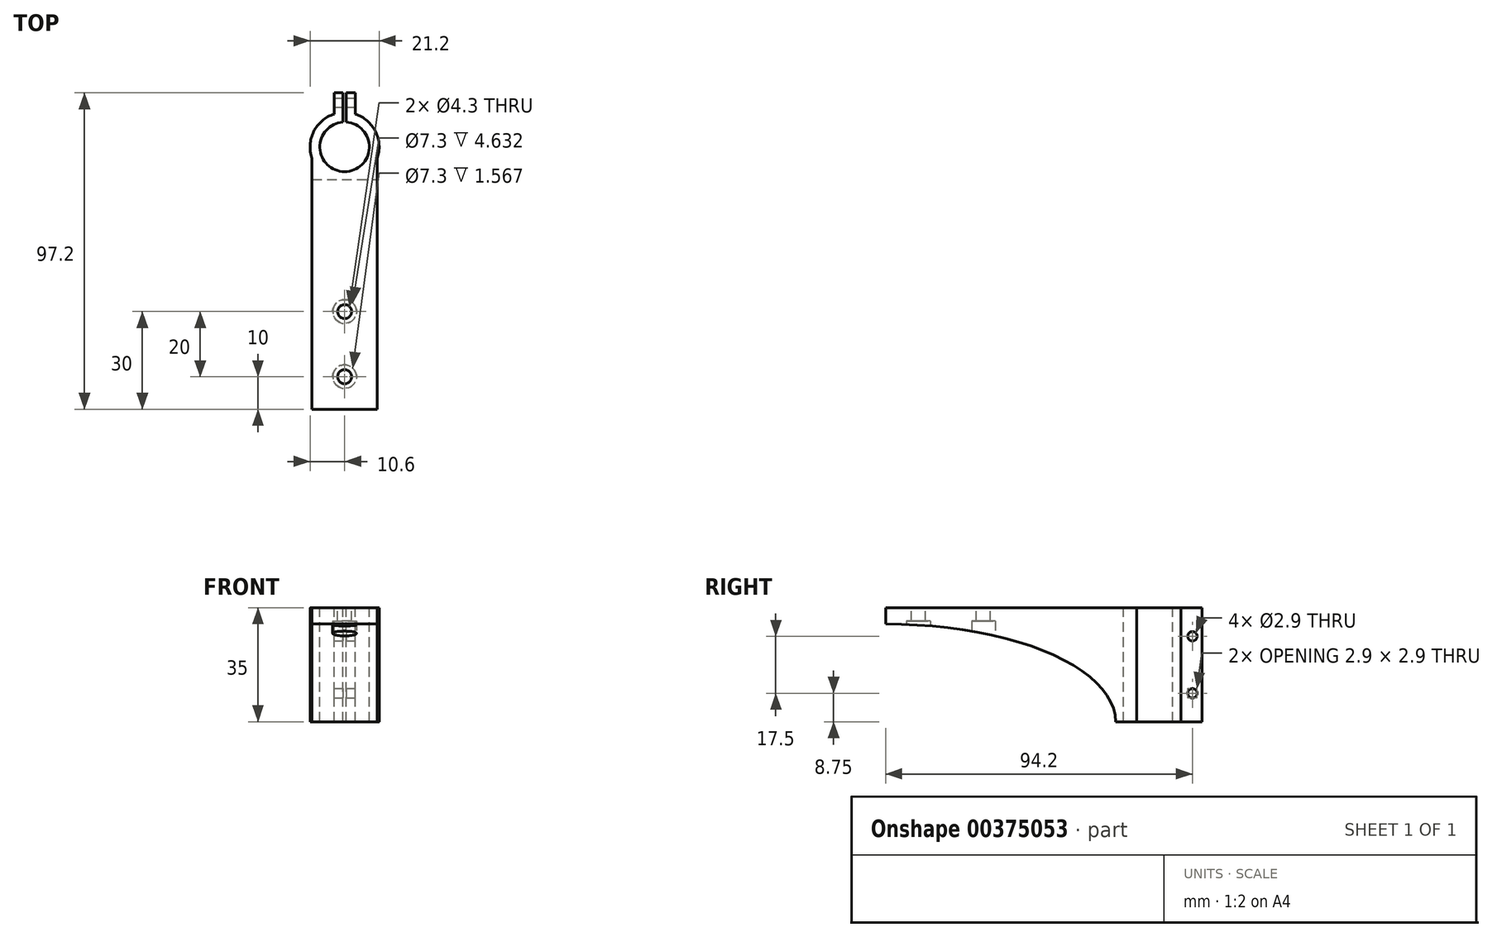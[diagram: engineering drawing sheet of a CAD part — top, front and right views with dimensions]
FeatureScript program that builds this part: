
annotation { "Feature Type Name" : "Feature", "Feature Type Description" : "" }
export const myFeature = defineFeature(function(context is Context, id is Id, definition is map)
    precondition{}
    {
        {
            var Q0;
            Q0=qCreatedBy(makeId("Top.planeOp"),FACE);
            var sketch = newSketch(context, id + "F0", { "sketchPlane" : qUnion([Q0])});
            skCircle(sketch, "E0", {"center": v(0, 0) * mm, "radius": 7.6 * mm});
            skArc(sketch, "E1.0", {"start": v(-3.25, 10.09) * mm, "mid": v(0, -10.6) * mm, "end": v(3.25, 10.09) * mm});
            skLineSegment(sketch, "E2.top", {"start": v(3.25, 16.6) * mm, "end": v(-3.25, 16.6) * mm});
            skLineSegment(sketch, "E2.left", {"start": v(3.25, 10.09) * mm, "end": v(3.25, 16.6) * mm});
            skLineSegment(sketch, "E2.right", {"start": v(-3.25, 10.09) * mm, "end": v(-3.25, 16.6) * mm});
            skPoint(sketch, "E2.middle", {"position": v(0, 10.6) * mm});
            skLineSegment(sketch, "E3.top", {"start": v(-10, -80.6) * mm, "end": v(10, -80.6) * mm});
            skLineSegment(sketch, "E3.left", {"start": v(-10, -3.52) * mm, "end": v(-10, -80.6) * mm});
            skLineSegment(sketch, "E3.right", {"start": v(10, -3.52) * mm, "end": v(10, -80.6) * mm});
            skSolve(sketch);
        }
        {
            var Q0;
            Q0=makeQuery(id+"F0.imprint","IMPRINT",FACE,{"disambiguationData":[TD([[makeQuery(id+"F0.imprint","IMPRINT",EDGE,{"derivedFrom":sQuery(id+"F0.wireOp",EDGE,"E3.top")}),1.0]])]});
            extrude(context, id + "F1", {"entities" : qUnion([Q0]), "oppositeDirection" : true, "depth" : 35 * mm});
        }
        {
            var Q0;
            Q0=makeQuery(id+"F0.imprint","IMPRINT",FACE,{"disambiguationData":[TD([[makeQuery(id+"F0.imprint","IMPRINT",EDGE,{"derivedFrom":sQuery(id+"F0.wireOp",EDGE,"E0")}),-1.0]])]});
            extrude(context, id + "F2", {"entities" : qUnion([Q0]), "operationType" : NewBodyOperationType.ADD, "oppositeDirection" : true, "depth" : 35 * mm});
        }
        {
            var Q0;
            {var subQ0=sQuery(id+"F0.wireOp",EDGE,"E1.0");Q0=makeQuery(id+"F2.boolean.opBoolean","MERGE",FACE,{"derivedFrom":[makeQuery(id+"F1.opExtrude","CAP_FACE",FACE,{"disambiguationData":[OSD([subQ0,sQuery(id+"F0.wireOp",EDGE,"E3.top"),sQuery(id+"F0.wireOp",EDGE,"E3.left"),sQuery(id+"F0.wireOp",EDGE,"E3.right")])],"isStart":true}),makeQuery(id+"F2.opExtrude","CAP_FACE",FACE,{"disambiguationData":[OSD([sQuery(id+"F0.wireOp",EDGE,"E0"),subQ0,sQuery(id+"F0.wireOp",EDGE,"E2.top"),sQuery(id+"F0.wireOp",EDGE,"E2.left"),sQuery(id+"F0.wireOp",EDGE,"E2.right")])],"isStart":true})]});}
            var sketch = newSketch(context, id + "F3", { "sketchPlane" : qUnion([Q0])});
            skCircle(sketch, "E4", {"center": v(0, -50.6) * mm, "radius": 2.15 * mm});
            skCircle(sketch, "E5", {"center": v(0, -70.6) * mm, "radius": 2.15 * mm});
            skSolve(sketch);
        }
        {
            var Q0;
            Q0=qSketchRegion(id+"F3",true);
            extrude(context, id + "F4", {"entities" : qUnion([Q0]), "operationType" : NewBodyOperationType.REMOVE, "endBound" : BoundingType.THROUGH_ALL, "oppositeDirection" : true, "depth" : 25 * mm});
        }
        {
            var Q0;
            Q0=makeQuery(id+"F1.opExtrude","CAP_FACE",FACE,{"disambiguationData":[OSD([sQuery(id+"F0.wireOp",EDGE,"E0"),sQuery(id+"F0.wireOp",EDGE,"E1.0"),sQuery(id+"F0.wireOp",EDGE,"E2.top"),sQuery(id+"F0.wireOp",EDGE,"E2.left"),sQuery(id+"F0.wireOp",EDGE,"E2.right"),sQuery(id+"F0.wireOp",EDGE,"E3.top"),sQuery(id+"F0.wireOp",EDGE,"E3.left"),sQuery(id+"F0.wireOp",EDGE,"E3.right")])],"isStart":false});
            var sketch = newSketch(context, id + "F5", { "sketchPlane" : qUnion([Q0])});
            skCircle(sketch, "E6", {"center": v(0, 70.6) * mm, "radius": 3.65 * mm});
            skCircle(sketch, "E7", {"center": v(0, 50.6) * mm, "radius": 3.65 * mm});
            skSolve(sketch);
        }
        {
            var Q0;
            Q0=makeQuery(id+"F5.imprint","IMPRINT",FACE,{"disambiguationData":[TD([[makeQuery(id+"F5.imprint","IMPRINT",EDGE,{"derivedFrom":sQuery(id+"F5.wireOp",EDGE,"E6")}),1.0]])]});
            var Q1;
            Q1=makeQuery(id+"F5.imprint","IMPRINT",FACE,{"disambiguationData":[TD([[makeQuery(id+"F5.imprint","IMPRINT",EDGE,{"derivedFrom":sQuery(id+"F5.wireOp",EDGE,"E7")}),1.0]])]});
            extrude(context, id + "F6", {"entities" : qUnion([Q0, Q1]), "operationType" : NewBodyOperationType.REMOVE, "oppositeDirection" : true, "depth" : 31 * mm});
        }
        {
            var Q0;
            Q0=makeQuery(id+"F1.opExtrude","SWEPT_FACE",FACE,{"disambiguationData":[OSD([sQuery(id+"F0.wireOp",EDGE,"E3.right")])]});
            var sketch = newSketch(context, id + "F7", { "sketchPlane" : qUnion([Q0])});
            skLineSegment(sketch, "E8", {"start": v(-3.52, -35) * mm, "end": v(-10.02, -35) * mm});
            skLineSegment(sketch, "E9", {"start": v(-80.6, 0) * mm, "end": v(-80.6, -5) * mm});
            skEllipse(sketch, "E10", {"center": v(-80.6, -35) * mm, "majorRadius": 70.58 * mm, "minorRadius": 30 * mm, "majorAxis": v(1, 0)});
            skSolve(sketch);
        }
        {
            var Q0;
            {var subQ1=sQuery(id+"F0.wireOp",EDGE,"E3.right");var subQ2=makeQuery(id+"F1.opExtrude","SWEPT_EDGE",EDGE,{"disambiguationData":[OSD([sQuery(id+"F0.wireOp",EDGE,"E3.top"),subQ1])]});var subQ4=makeQuery(id+"F1.opExtrude","CAP_EDGE",EDGE,{"disambiguationData":[OSD([subQ1])],"isStart":false});var subQ6=makeQuery(id+"F7.imprint","INTERSECT",VERTEX,{"derivedFrom":[subQ2,subQ4]});Q0=makeQuery(id+"F7.imprint","IMPRINT",FACE,{"disambiguationData":[TD([[makeQuery(id+"F7.imprint","IMPRINT",EDGE,{"disambiguationData":[TD([[subQ6,1.0]])],"derivedFrom":subQ4}),-1.0]])]});}
            extrude(context, id + "F8", {"entities" : qUnion([Q0]), "operationType" : NewBodyOperationType.REMOVE, "endBound" : BoundingType.THROUGH_ALL, "oppositeDirection" : true, "depth" : 25 * mm});
        }
        {
            var Q0;
            Q0=makeQuery(id+"F1.opExtrude","CAP_FACE",FACE,{"disambiguationData":[OSD([sQuery(id+"F0.wireOp",EDGE,"E0"),sQuery(id+"F0.wireOp",EDGE,"E1.0"),sQuery(id+"F0.wireOp",EDGE,"E2.top"),sQuery(id+"F0.wireOp",EDGE,"E2.left"),sQuery(id+"F0.wireOp",EDGE,"E2.right"),sQuery(id+"F0.wireOp",EDGE,"E3.top"),sQuery(id+"F0.wireOp",EDGE,"E3.left"),sQuery(id+"F0.wireOp",EDGE,"E3.right")])],"isStart":true});
            var sketch = newSketch(context, id + "F9", { "sketchPlane" : qUnion([Q0])});
            skLineSegment(sketch, "E11.bottom", {"start": v(0, 18.6) * mm, "end": v(-0.5, 18.6) * mm});
            skLineSegment(sketch, "E11.top", {"start": v(0, 0) * mm, "end": v(-0.5, 0) * mm});
            skLineSegment(sketch, "E11.left", {"start": v(0, 18.6) * mm, "end": v(0, 0) * mm});
            skLineSegment(sketch, "E11.right", {"start": v(-0.5, 18.6) * mm, "end": v(-0.5, 0) * mm});
            skLineSegment(sketch, "E12.MirrorCS", {"start": v(0.5, 18.6) * mm, "end": v(0.5, 0) * mm});
            skLineSegment(sketch, "E13.MirrorCS", {"start": v(0, 0) * mm, "end": v(0.5, 0) * mm});
            skLineSegment(sketch, "E14.MirrorCS", {"start": v(0, 18.6) * mm, "end": v(0.5, 18.6) * mm});
            skSolve(sketch);
        }
        {
            var Q0;
            {var subQ0=sQuery(id+"F9.wireOp",EDGE,"E11.left");var subQ1=makeQuery(id+"F2.opExtrude","CAP_EDGE",EDGE,{"disambiguationData":[OSD([sQuery(id+"F0.wireOp",EDGE,"E2.top")])],"isStart":true});var subQ2=makeQuery(id+"F9.imprint","INTERSECT",VERTEX,{"derivedFrom":[subQ1,subQ0]});Q0=makeQuery(id+"F9.imprint","IMPRINT",FACE,{"disambiguationData":[TD([[makeQuery(id+"F9.imprint","IMPRINT",EDGE,{"disambiguationData":[TD([[subQ2,-1.0]])],"derivedFrom":subQ0}),1.0]])]});}
            var Q1;
            {var subQ0=sQuery(id+"F9.wireOp",EDGE,"E11.top");Q1=makeQuery(id+"F9.imprint","IMPRINT",FACE,{"disambiguationData":[TD([[makeQuery(id+"F9.imprint","IMPRINT",EDGE,{"derivedFrom":subQ0}),-1.0]])]});}
            var Q2;
            {var subQ0=sQuery(id+"F9.wireOp",EDGE,"E11.bottom");Q2=makeQuery(id+"F9.imprint","IMPRINT",FACE,{"disambiguationData":[TD([[makeQuery(id+"F9.imprint","IMPRINT",EDGE,{"derivedFrom":subQ0}),1.0]])]});}
            var Q3;
            {var subQ0=sQuery(id+"F9.wireOp",EDGE,"E14.MirrorCS");Q3=makeQuery(id+"F9.imprint","IMPRINT",FACE,{"disambiguationData":[TD([[makeQuery(id+"F9.imprint","IMPRINT",EDGE,{"derivedFrom":subQ0}),-1.0]])]});}
            var Q4;
            {var subQ0=sQuery(id+"F9.wireOp",EDGE,"E13.MirrorCS");Q4=makeQuery(id+"F9.imprint","IMPRINT",FACE,{"disambiguationData":[TD([[makeQuery(id+"F9.imprint","IMPRINT",EDGE,{"derivedFrom":subQ0}),1.0]])]});}
            var Q5;
            {var subQ0=sQuery(id+"F9.wireOp",EDGE,"E11.left");var subQ1=makeQuery(id+"F2.opExtrude","CAP_EDGE",EDGE,{"disambiguationData":[OSD([sQuery(id+"F0.wireOp",EDGE,"E2.top")])],"isStart":true});var subQ2=makeQuery(id+"F9.imprint","INTERSECT",VERTEX,{"derivedFrom":[subQ1,subQ0]});Q5=makeQuery(id+"F9.imprint","IMPRINT",FACE,{"disambiguationData":[TD([[makeQuery(id+"F9.imprint","IMPRINT",EDGE,{"disambiguationData":[TD([[subQ2,-1.0]])],"derivedFrom":subQ0}),-1.0]])]});}
            extrude(context, id + "F10", {"entities" : qUnion([Q0, Q1, Q2, Q3, Q4, Q5]), "operationType" : NewBodyOperationType.REMOVE, "endBound" : BoundingType.THROUGH_ALL, "oppositeDirection" : true, "depth" : 25 * mm});
        }
        {
            var Q0;
            Q0=makeQuery(id+"F2.opExtrude","SWEPT_FACE",FACE,{"disambiguationData":[OSD([sQuery(id+"F0.wireOp",EDGE,"E2.left")])]});
            var sketch = newSketch(context, id + "F11", { "sketchPlane" : qUnion([Q0])});
            skCircle(sketch, "E15", {"center": v(13.6, -8.75) * mm, "radius": 1.45 * mm});
            skCircle(sketch, "E16", {"center": v(13.6, -26.25) * mm, "radius": 1.45 * mm});
            skCircle(sketch, "E17.0", {"center": v(13.6, -8.75) * mm, "radius": 2.45 * mm});
            skCircle(sketch, "E18.0", {"center": v(13.6, -26.25) * mm, "radius": 2.45 * mm});
            skSolve(sketch);
        }
        {
            var Q0;
            Q0=makeQuery(id+"F11.imprint","IMPRINT",FACE,{"disambiguationData":[TD([[makeQuery(id+"F11.imprint","IMPRINT",EDGE,{"derivedFrom":sQuery(id+"F11.wireOp",EDGE,"E15")}),1.0]])]});
            var Q1;
            Q1=makeQuery(id+"F11.imprint","IMPRINT",FACE,{"disambiguationData":[TD([[makeQuery(id+"F11.imprint","IMPRINT",EDGE,{"derivedFrom":sQuery(id+"F11.wireOp",EDGE,"E16")}),1.0]])]});
            extrude(context, id + "F12", {"entities" : qUnion([Q0, Q1]), "operationType" : NewBodyOperationType.REMOVE, "endBound" : BoundingType.THROUGH_ALL, "oppositeDirection" : true, "depth" : 25 * mm});
        }
    });
